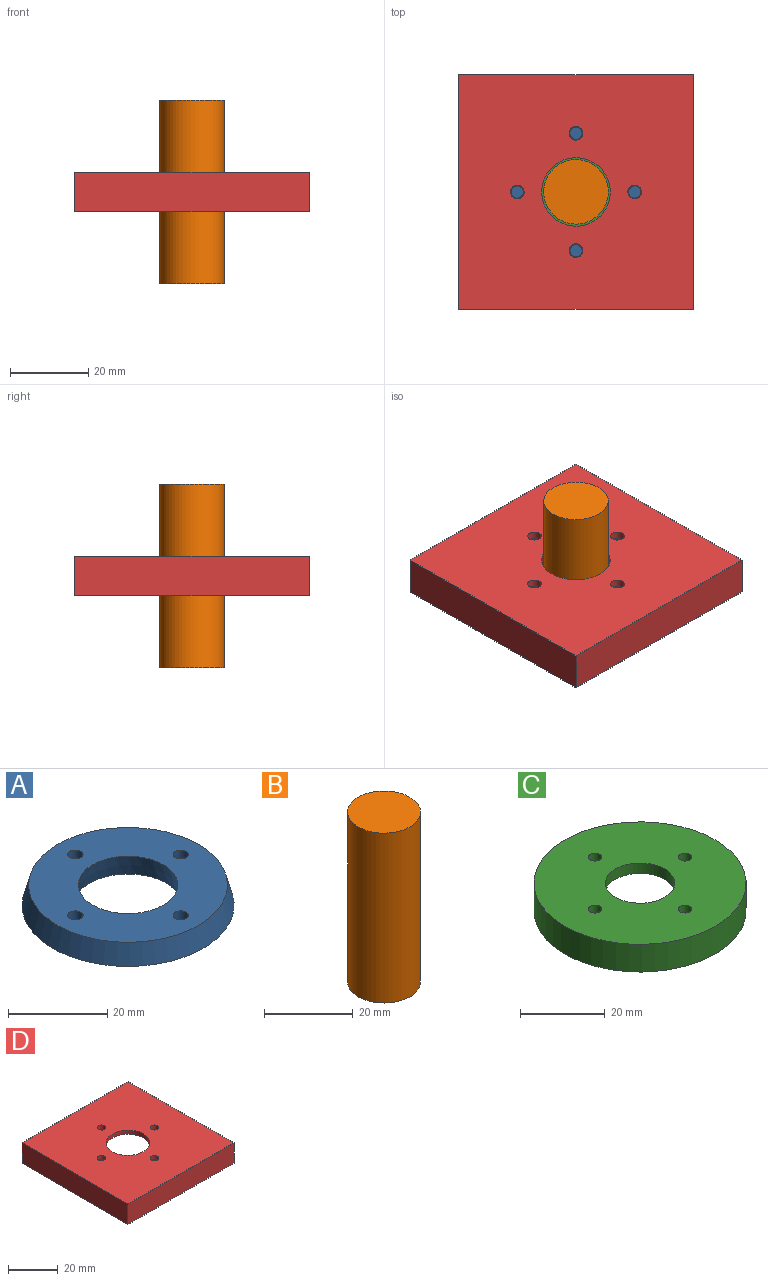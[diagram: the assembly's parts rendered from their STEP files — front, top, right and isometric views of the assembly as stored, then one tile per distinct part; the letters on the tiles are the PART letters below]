
ASSEMBLY  parts=4 mates=5
PART A: 12 faces, bbox 42.7x42.7x5 mm
  f0: cylinder r=1.55mm len=3.1mm, axis (0,0,-1), area 24.3mm2, adj f1,f9
  f1: plane 3.1x3.1mm, normal (0,0,1), area 7.5mm2, adj f0
  f2: cylinder r=1.55mm len=3.1mm, axis (0,0,-1), area 24.3mm2, adj f3,f9
  f3: plane 3.1x3.1mm, normal (0,0,1), area 7.5mm2, adj f2
  f4: cylinder r=1.55mm len=3.1mm, axis (0,0,-1), area 24.3mm2, adj f5,f9
  f5: plane 3.1x3.1mm, normal (0,0,1), area 7.5mm2, adj f4
  f6: cone r=10mm half-angle=10deg, axis (0,0,-1), area 333.1mm2, adj f7,f9
  f7: plane 42.68x42.68mm, normal (0,0,-1), area 1058.6mm2, adj f6,f8
  f8: cone r=21.34mm half-angle=15deg, axis (0,0,-1), area 672.3mm2, adj f7,f9
  f9: plane 40x40mm, normal (0,0,1), area 912.3mm2, adj f0,f2,f4,f6,f8,f11
  f10: plane 3.1x3.1mm, normal (0,0,1), area 7.5mm2, adj f11
  f11: cylinder r=1.55mm len=3.1mm, axis (0,0,-1), area 24.3mm2, adj f9,f10
PART B: 3 faces, bbox 16.5x16.5x47 mm
  f0: cylinder r=8.25mm len=47mm, axis (0,0,-1), area 2436.3mm2, adj f1,f2
  f1: plane 16.5x16.5mm, normal (0,0,1), area 213.8mm2, adj f0
  f2: plane 16.5x16.5mm, normal (0,0,-1), area 213.8mm2, adj f0
PART C: 10 faces, bbox 50x50x8 mm
  f0: cylinder r=1.6mm len=3.2mm, axis (0,0,-1), area 30.2mm2, adj f3,f5
  f1: cylinder r=1.6mm len=3.2mm, axis (0,0,-1), area 30.2mm2, adj f3,f5
  f2: cylinder r=1.6mm len=3.2mm, axis (0,0,-1), area 30.2mm2, adj f3,f5
  f3: plane 40x40mm, normal (0,0,-1), area 1013.2mm2, adj f0,f1,f2,f4,f8,f9
  f4: cylinder r=8.2mm len=16.4mm, axis (0,0,1), area 154.6mm2, adj f3,f5
  f5: plane 50x50mm, normal (0,0,1), area 1720.1mm2, adj f0,f1,f2,f4,f6,f9
  f6: cylinder r=25mm len=50mm, axis (0,0,1), area 1256.6mm2, adj f5,f7
  f7: plane 50x50mm, normal (0,0,-1), area 532.9mm2, adj f6,f8
  f8: cone r=20mm half-angle=15deg, axis (0,0,-1), area 672.3mm2, adj f3,f7
  f9: cylinder r=1.6mm len=3.2mm, axis (0,0,-1), area 30.2mm2, adj f3,f5
PART D: 13 faces, bbox 60x60x10 mm
  f0: cylinder r=1.75mm len=3.5mm, axis (0,0,1), area 22mm2, adj f3,f9
  f1: cylinder r=1.75mm len=3.5mm, axis (0,0,1), area 22mm2, adj f3,f9
  f2: cylinder r=1.75mm len=3.5mm, axis (0,0,1), area 22mm2, adj f3,f9
  f3: plane 50x50mm, normal (0,0,-1), area 1684.5mm2, adj f0,f1,f2,f7,f10,f12
  f4: plane 60x10mm, normal (0,1,0), area 600mm2, adj f5,f8,f9,f11
  f5: plane 60x10mm, normal (-1,0,0), area 600mm2, adj f4,f6,f9,f11
  f6: plane 60x10mm, normal (0,-1,0), area 600mm2, adj f5,f8,f9,f11
  f7: cylinder r=8.75mm len=17.5mm, axis (0,0,-1), area 110mm2, adj f3,f9
  f8: plane 60x10mm, normal (1,0,0), area 600mm2, adj f4,f6,f9,f11
  f9: plane 60x60mm, normal (0,0,1), area 3321mm2, adj f0,f1,f2,f4,f5,f6,f7,f8
  f10: cylinder r=25mm len=50mm, axis (0,0,1), area 1256.6mm2, adj f3,f11
  f11: plane 60x60mm, normal (0,0,-1), area 1636.5mm2, adj f4,f5,f6,f8,f10
  f12: cylinder r=1.75mm len=3.5mm, axis (0,0,1), area 22mm2, adj f3,f9
PLACE A t=(-8.27,2.26,-2.99)mm
PLACE B t=(-8.27,2.26,-23.99)mm
PLACE C t=(-8.27,2.26,-0.49)mm
PLACE D t=(-8.27,2.26,2.51)mm fixed
MATE slider B.f0 <-> A.f6  axis (0,0,-1) through (-8.27,2.26,-0.49)mm
MATE slider D.f7 <-> B.f0  axis (0,0,-1) through (-8.27,2.26,3.51)mm
MATE slider A.f2 <-> C.f1  axis (0,0,1) through (-8.27,-12.74,-0.49)mm
MATE slider D.f10 <-> C.f4  axis (0,0,1) through (-8.27,2.26,-1.49)mm
MATE planar C.f1 <-> D.f10  axis (0,0,1) through (-8.27,-12.74,2.51)mm
